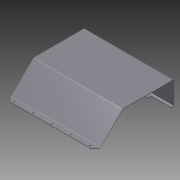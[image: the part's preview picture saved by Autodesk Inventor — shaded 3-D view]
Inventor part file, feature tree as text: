
AUTODESK INVENTOR PART (.ipt)
format: ipt  version: 2014 (Build 180170000, 170)  size: 218,112 bytes
history: native  units: mm
features: other x7, sketch x4, plane x2, hole x2, chamfer x1, reference x1
ambient origin geometry x8: Origin, YZ Plane, XZ Plane, XY Plane, X Axis, Y Axis, Z Axis, Center Point
bodies: Body1 (feature_tree)
feature tree (17):
  other  "Sólido1"
  plane  "Plano de trabajo2"
  other  "Cara1"
  plane  "Plano de trabajo3"
  other  "Pestaña de contorno6"
  sketch  "Boceto5"  dims[d5=1.5mm]
  hole  "Agujero1"  [1 undecoded]
  chamfer  "Chaflán de esquina1"  Distance=200.0mm
  sketch  "Boceto2"  dims[d2=110.0mm d3=55.0mm]
  other  "Placa1"
  sketch  "Boceto4"  dims[d4=8.0mm]
  other  "Placa8"
  other  "Doblez7"
  sketch  "Boceto6"  dims[d30=100.0mm d31=200.0mm d32=5.0mm d42=50.0mm d89=12.5mm d90=80.0mm d93=1.5mm d94=0.75mm d95=3.0mm d96=1.5mm d97=1.5mm d98=1.5mm d99=6.0mm d100=1.5mm d101=1.5mm d102=4.0mm d103=4.0mm d104=4.0mm d105=4.0mm d107=15.0mm d108=42.5mm d109=42.5mm d111=15.0mm d112=4.0mm d113=42.5mm d114=3.2mm d115=6.0mm d116=4.0mm d117=2.0mm d118=90.0deg d119=8.0mm d120=0.0mm d121=10.0mm d122=6.0mm d123=45.0deg d124=45.0deg d126=1.5mm d127=1.5mm d128=0.0mm]
  hole  "Hole1"  [1 undecoded]
  reference  "Referencia6"
  other  "Definición1"
note: 2 required parameter values undecoded (feature->parameter linkage not recoverable at this tier; creation-order binding heuristic only, values carry confidence <= 0.55)
